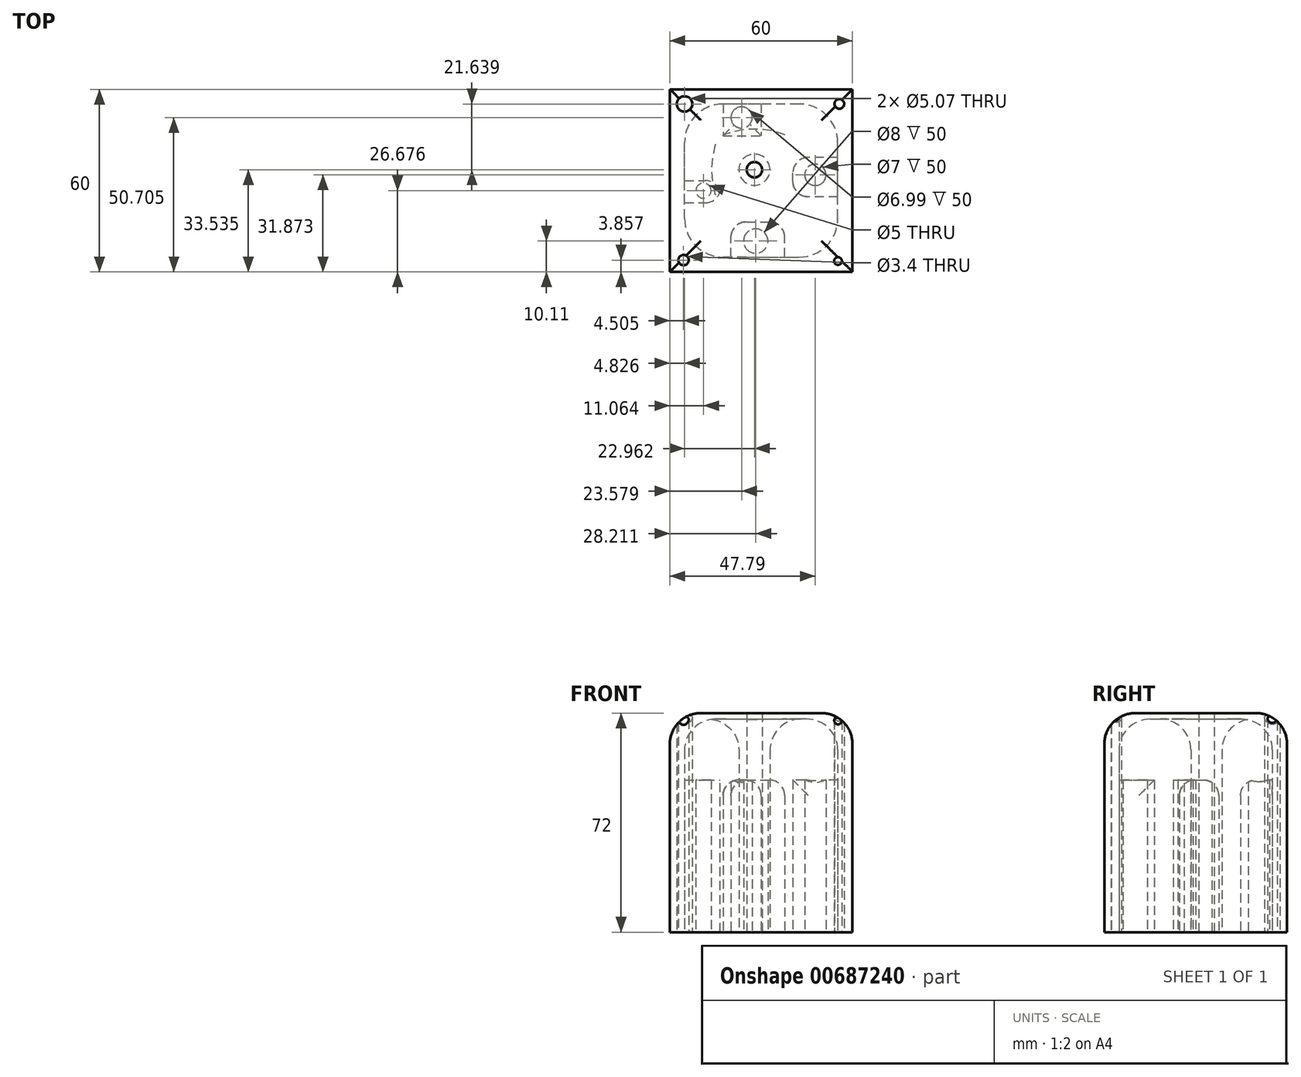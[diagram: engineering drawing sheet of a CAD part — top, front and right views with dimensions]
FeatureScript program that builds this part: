
annotation { "Feature Type Name" : "Feature", "Feature Type Description" : "" }
export const myFeature = defineFeature(function(context is Context, id is Id, definition is map)
    precondition{}
    {
        {
            var Q0;
            Q0=qCreatedBy(makeId("Top.planeOp"),FACE);
            var sketch = newSketch(context, id + "F0", { "sketchPlane" : qUnion([Q0])});
            skLineSegment(sketch, "E0.bottom", {"start": v(0, 0) * mm, "end": v(-60, 0) * mm});
            skLineSegment(sketch, "E0.top", {"start": v(0, 60) * mm, "end": v(-60, 60) * mm});
            skLineSegment(sketch, "E0.left", {"start": v(0, 0) * mm, "end": v(0, 60) * mm});
            skLineSegment(sketch, "E0.right", {"start": v(-60, 0) * mm, "end": v(-60, 60) * mm});
            skLineSegment(sketch, "E1.1", {"start": v(-4.83, 4.83) * mm, "end": v(-4.83, 24.65) * mm});
            skLineSegment(sketch, "E1.3", {"start": v(-55.17, 4.83) * mm, "end": v(-55.17, 22.68) * mm});
            skLineSegment(sketch, "E2.top", {"start": v(-39.92, 16.43) * mm, "end": v(-22.26, 16.43) * mm});
            skLineSegment(sketch, "E2.left", {"start": v(-39.92, 4.83) * mm, "end": v(-39.92, 16.43) * mm});
            skLineSegment(sketch, "E2.right", {"start": v(-22.26, 4.83) * mm, "end": v(-22.26, 16.43) * mm});
            skLineSegment(sketch, "E3.bottom", {"start": v(-4.83, 24.65) * mm, "end": v(-19.6, 24.65) * mm});
            skLineSegment(sketch, "E3.top", {"start": v(-4.83, 37.6) * mm, "end": v(-19.6, 37.6) * mm});
            skLineSegment(sketch, "E3.right", {"start": v(-19.6, 24.65) * mm, "end": v(-19.6, 37.6) * mm});
            skPoint(sketch, "E4.oppositeSnap0", {"position": v(-30, 55.17) * mm});
            skLineSegment(sketch, "E4.top", {"start": v(-42.54, 44.73) * mm, "end": v(-30, 44.73) * mm});
            skLineSegment(sketch, "E4.left", {"start": v(-42.54, 55.17) * mm, "end": v(-42.54, 44.73) * mm});
            skLineSegment(sketch, "E4.right", {"start": v(-30, 55.17) * mm, "end": v(-30, 44.73) * mm});
            skPoint(sketch, "E5.oppositeSnap0", {"position": v(-55.17, 30) * mm});
            skLineSegment(sketch, "E5.bottom", {"start": v(-55.17, 22.68) * mm, "end": v(-43.31, 22.68) * mm});
            skLineSegment(sketch, "E5.top", {"start": v(-55.17, 30) * mm, "end": v(-43.31, 30) * mm});
            skLineSegment(sketch, "E5.right", {"start": v(-43.31, 22.68) * mm, "end": v(-43.31, 30) * mm});
            skLineSegment(sketch, "E6.trimOffspring", {"start": v(-55.17, 30) * mm, "end": v(-55.17, 55.17) * mm});
            skLineSegment(sketch, "E7.trimOffspring", {"start": v(-39.92, 4.83) * mm, "end": v(-55.17, 4.83) * mm});
            skLineSegment(sketch, "E8.trimOffspring", {"start": v(-4.83, 37.6) * mm, "end": v(-4.83, 55.17) * mm});
            skLineSegment(sketch, "E9.trimOffspring", {"start": v(-42.54, 55.17) * mm, "end": v(-55.17, 55.17) * mm});
            skLineSegment(sketch, "E10", {"start": v(-22.26, 4.83) * mm, "end": v(-4.83, 4.83) * mm});
            skLineSegment(sketch, "E11", {"start": v(-4.83, 55.17) * mm, "end": v(-30, 55.17) * mm});
            skCircle(sketch, "E12", {"center": v(-31.79, 10.1) * mm, "radius": 4 * mm});
            skCircle(sketch, "E13", {"center": v(-12.21, 31.87) * mm, "radius": 3.5 * mm});
            skPoint(sketch, "E13.centerSnap0", {"position": v(-12.21, 24.65) * mm});
            skCircle(sketch, "E14", {"center": v(-36.42, 50.7) * mm, "radius": 3.5 * mm});
            skCircle(sketch, "E15", {"center": v(-48.94, 26.68) * mm, "radius": 2.5 * mm});
            skSolve(sketch);
        }
        {
            var Q0;
            Q0 = qSketchRegion(id + "F0", true);
            extrude(context, id + "F1", {"entities" : qUnion([Q0]), "depth" : 50 * mm, "offsetDistance" : 25.4 * mm});
        }
        {
            var Q0;
            Q0=makeQuery(id+"F1.opExtrude","SWEPT_EDGE",EDGE,{"disambiguationData":[OSD([sQuery(id+"F0.wireOp",EDGE,"E5.top"),sQuery(id+"F0.wireOp",EDGE,"E5.right")])]});
            var Q1;
            Q1=makeQuery(id+"F1.opExtrude","SWEPT_EDGE",EDGE,{"disambiguationData":[OSD([sQuery(id+"F0.wireOp",EDGE,"E5.bottom"),sQuery(id+"F0.wireOp",EDGE,"E5.right")])]});
            var Q2;
            Q2=makeQuery(id+"F1.opExtrude","CAP_EDGE",EDGE,{"disambiguationData":[OSD([sQuery(id+"F0.wireOp",EDGE,"E4.top")])],"isStart":false});
            var Q3;
            Q3=makeQuery(id+"F1.opExtrude","CAP_EDGE",EDGE,{"disambiguationData":[OSD([sQuery(id+"F0.wireOp",EDGE,"E3.top")])],"isStart":false});
            var Q4;
            Q4=makeQuery(id+"F1.opExtrude","CAP_EDGE",EDGE,{"disambiguationData":[OSD([sQuery(id+"F0.wireOp",EDGE,"E4.left")])],"isStart":false});
            var Q5;
            Q5=makeQuery(id+"F1.opExtrude","CAP_EDGE",EDGE,{"disambiguationData":[OSD([sQuery(id+"F0.wireOp",EDGE,"E4.right")])],"isStart":false});
            var Q6;
            Q6=makeQuery(id+"F1.opExtrude","SWEPT_EDGE",EDGE,{"disambiguationData":[OSD([sQuery(id+"F0.wireOp",EDGE,"E3.bottom"),sQuery(id+"F0.wireOp",EDGE,"E3.right")])]});
            var Q7;
            Q7=makeQuery(id+"F1.opExtrude","SWEPT_EDGE",EDGE,{"disambiguationData":[OSD([sQuery(id+"F0.wireOp",EDGE,"E3.top"),sQuery(id+"F0.wireOp",EDGE,"E3.right")])]});
            var Q8;
            Q8=makeQuery(id+"F1.opExtrude","CAP_EDGE",EDGE,{"disambiguationData":[OSD([sQuery(id+"F0.wireOp",EDGE,"E3.bottom")])],"isStart":false});
            var Q9;
            Q9=makeQuery(id+"F1.opExtrude","SWEPT_EDGE",EDGE,{"disambiguationData":[OSD([sQuery(id+"F0.wireOp",EDGE,"E2.top"),sQuery(id+"F0.wireOp",EDGE,"E2.left")])]});
            var Q10;
            Q10=makeQuery(id+"F1.opExtrude","SWEPT_EDGE",EDGE,{"disambiguationData":[OSD([sQuery(id+"F0.wireOp",EDGE,"E2.top"),sQuery(id+"F0.wireOp",EDGE,"E2.right")])]});
            var Q11;
            Q11=makeQuery(id+"F1.opExtrude","CAP_EDGE",EDGE,{"disambiguationData":[OSD([sQuery(id+"F0.wireOp",EDGE,"E2.right")])],"isStart":false});
            var Q12;
            Q12=makeQuery(id+"F1.opExtrude","CAP_EDGE",EDGE,{"disambiguationData":[OSD([sQuery(id+"F0.wireOp",EDGE,"E2.left")])],"isStart":false});
            fillet(context, id + "F2", {"entities" : qUnion([Q0, Q1, Q2, Q3, Q4, Q5, Q6, Q7, Q8, Q9, Q10, Q11, Q12]), "radius" : 5.08 * mm, "tangentPropagation" : true, "allowEdgeOverflow" : false});
        }
        {
            var Q0;
            Q0=makeQuery(id+"F2.opFillet","SPLIT",FACE,{"disambiguationData":[OD(1.0)],"derivedFrom":makeQuery(id+"F1.opExtrude","CAP_FACE",FACE,{"disambiguationData":[OSD([sQuery(id+"F0.wireOp",EDGE,"E0.bottom"),sQuery(id+"F0.wireOp",EDGE,"E0.top"),sQuery(id+"F0.wireOp",EDGE,"E0.left"),sQuery(id+"F0.wireOp",EDGE,"E0.right"),sQuery(id+"F0.wireOp",EDGE,"E1.1"),sQuery(id+"F0.wireOp",EDGE,"E1.3"),sQuery(id+"F0.wireOp",EDGE,"E2.top"),sQuery(id+"F0.wireOp",EDGE,"E2.left"),sQuery(id+"F0.wireOp",EDGE,"E2.right"),sQuery(id+"F0.wireOp",EDGE,"E3.bottom"),sQuery(id+"F0.wireOp",EDGE,"E3.top"),sQuery(id+"F0.wireOp",EDGE,"E3.right"),sQuery(id+"F0.wireOp",EDGE,"E4.top"),sQuery(id+"F0.wireOp",EDGE,"E4.left"),sQuery(id+"F0.wireOp",EDGE,"E4.right"),sQuery(id+"F0.wireOp",EDGE,"E5.bottom"),sQuery(id+"F0.wireOp",EDGE,"E5.top"),sQuery(id+"F0.wireOp",EDGE,"E5.right"),sQuery(id+"F0.wireOp",EDGE,"E6.trimOffspring"),sQuery(id+"F0.wireOp",EDGE,"E7.trimOffspring"),sQuery(id+"F0.wireOp",EDGE,"E8.trimOffspring"),sQuery(id+"F0.wireOp",EDGE,"E9.trimOffspring"),sQuery(id+"F0.wireOp",EDGE,"E10"),sQuery(id+"F0.wireOp",EDGE,"E11"),sQuery(id+"F0.wireOp",EDGE,"E12"),sQuery(id+"F0.wireOp",EDGE,"E13"),sQuery(id+"F0.wireOp",EDGE,"E14"),sQuery(id+"F0.wireOp",EDGE,"E15")])],"isStart":false})});
            var sketch = newSketch(context, id + "F3", { "sketchPlane" : qUnion([Q0])});
            skLineSegment(sketch, "E16.bottom", {"start": v(-60, 0) * mm, "end": v(0, 0) * mm});
            skLineSegment(sketch, "E16.top", {"start": v(-60, 60) * mm, "end": v(0, 60) * mm});
            skLineSegment(sketch, "E16.left", {"start": v(-60, 0) * mm, "end": v(-60, 60) * mm});
            skLineSegment(sketch, "E16.right", {"start": v(0, 0) * mm, "end": v(0, 60) * mm});
            skLineSegment(sketch, "E17.bottom", {"start": v(-55.17, 4.83) * mm, "end": v(-4.83, 4.83) * mm});
            skLineSegment(sketch, "E17.top", {"start": v(-55.17, 55.17) * mm, "end": v(-4.83, 55.17) * mm});
            skLineSegment(sketch, "E17.left", {"start": v(-55.17, 4.83) * mm, "end": v(-55.17, 55.17) * mm});
            skLineSegment(sketch, "E17.right", {"start": v(-4.83, 4.83) * mm, "end": v(-4.83, 55.17) * mm});
            skSolve(sketch);
        }
        {
            var Q0;
            Q0 = qSketchRegion(id + "F3", true);
            extrude(context, id + "F4", {"entities" : qUnion([Q0]), "operationType" : NewBodyOperationType.ADD, "depth" : 20 * mm, "offsetDistance" : 25.4 * mm});
        }
        {
            var Q0;
            Q0=makeQuery(id+"F4.opExtrude","CAP_FACE",FACE,{"disambiguationData":[OSD([sQuery(id+"F3.wireOp",EDGE,"E16.bottom"),sQuery(id+"F3.wireOp",EDGE,"E16.top"),sQuery(id+"F3.wireOp",EDGE,"E16.left"),sQuery(id+"F3.wireOp",EDGE,"E16.right"),sQuery(id+"F3.wireOp",EDGE,"E17.bottom"),sQuery(id+"F3.wireOp",EDGE,"E17.top"),sQuery(id+"F3.wireOp",EDGE,"E17.left"),sQuery(id+"F3.wireOp",EDGE,"E17.right")])],"isStart":false});
            var sketch = newSketch(context, id + "F5", { "sketchPlane" : qUnion([Q0])});
            skLineSegment(sketch, "E18.bottom", {"start": v(-60, 0) * mm, "end": v(0, 0) * mm});
            skLineSegment(sketch, "E18.top", {"start": v(-60, 60) * mm, "end": v(0, 60) * mm});
            skLineSegment(sketch, "E18.left", {"start": v(-60, 0) * mm, "end": v(-60, 60) * mm});
            skLineSegment(sketch, "E18.right", {"start": v(0, 0) * mm, "end": v(0, 60) * mm});
            skSolve(sketch);
        }
        {
            var Q0;
            Q0 = qSketchRegion(id + "F5", true);
            extrude(context, id + "F6", {"entities" : qUnion([Q0]), "operationType" : NewBodyOperationType.ADD, "depth" : 2 * mm, "offsetDistance" : 25.4 * mm});
        }
        {
            var Q0;
            Q0=qCreatedBy(makeId("Top.planeOp"),FACE);
            var sketch = newSketch(context, id + "F7", { "sketchPlane" : qUnion([Q0])});
            skCircle(sketch, "E19", {"center": v(-32.21, 33.53) * mm, "radius": 5.11 * mm});
            skSolve(sketch);
        }
        {
            var Q0;
            Q0 = qSketchRegion(id + "F7", true);
            extrude(context, id + "F8", {"entities" : qUnion([Q0]), "operationType" : NewBodyOperationType.ADD, "depth" : 70 * mm, "offsetDistance" : 25.4 * mm});
        }
        {
            var Q0;
            Q0=makeQuery(id+"F4.opExtrude","CAP_EDGE",EDGE,{"disambiguationData":[OSD([sQuery(id+"F3.wireOp",EDGE,"E17.right")])],"isStart":false});
            var Q1;
            Q1=makeQuery(id+"F4.opExtrude","CAP_EDGE",EDGE,{"disambiguationData":[OSD([sQuery(id+"F3.wireOp",EDGE,"E17.bottom")])],"isStart":false});
            var Q2;
            Q2=makeQuery(id+"F4.opExtrude","CAP_EDGE",EDGE,{"disambiguationData":[OSD([sQuery(id+"F3.wireOp",EDGE,"E17.left")])],"isStart":false});
            var Q3;
            Q3=makeQuery(id+"F6.opExtrude","CAP_EDGE",EDGE,{"disambiguationData":[OSD([sQuery(id+"F5.wireOp",EDGE,"E18.right")])],"isStart":false});
            var Q4;
            Q4=makeQuery(id+"F6.opExtrude","CAP_EDGE",EDGE,{"disambiguationData":[OSD([sQuery(id+"F5.wireOp",EDGE,"E18.top")])],"isStart":false});
            var Q5;
            Q5=makeQuery(id+"F6.opExtrude","CAP_EDGE",EDGE,{"disambiguationData":[OSD([sQuery(id+"F5.wireOp",EDGE,"E18.left")])],"isStart":false});
            var Q6;
            Q6=makeQuery(id+"F6.opExtrude","CAP_EDGE",EDGE,{"disambiguationData":[OSD([sQuery(id+"F5.wireOp",EDGE,"E18.bottom")])],"isStart":false});
            var Q7;
            Q7=makeQuery(id+"F6.opExtrude","CAP_FACE",FACE,{"disambiguationData":[OSD([sQuery(id+"F5.wireOp",EDGE,"E18.bottom"),sQuery(id+"F5.wireOp",EDGE,"E18.top"),sQuery(id+"F5.wireOp",EDGE,"E18.left"),sQuery(id+"F5.wireOp",EDGE,"E18.right")])],"isStart":true});
            fillet(context, id + "F9", {"entities" : qUnion([Q0, Q1, Q2, Q3, Q4, Q5, Q6, Q7]), "radius" : 10.16 * mm, "tangentPropagation" : true, "allowEdgeOverflow" : false});
        }
        {
            var Q0;
            Q0=makeQuery(id+"F4.boolean.opBoolean","MERGE",EDGE,{"derivedFrom":[makeQuery(id+"F1.opExtrude","SWEPT_EDGE",EDGE,{"disambiguationData":[OSD([sQuery(id+"F0.wireOp",EDGE,"E1.3"),sQuery(id+"F0.wireOp",EDGE,"E7.trimOffspring")])]}),makeQuery(id+"F4.opExtrude","SWEPT_EDGE",EDGE,{"disambiguationData":[OSD([sQuery(id+"F3.wireOp",EDGE,"E17.bottom"),sQuery(id+"F3.wireOp",EDGE,"E17.left")])]})]});
            fillet(context, id + "F10", {"entities" : qUnion([Q0]), "radius" : 12.7 * mm, "tangentPropagation" : true, "allowEdgeOverflow" : false});
        }
        {
            var Q0;
            Q0=makeQuery(id+"F4.boolean.opBoolean","MERGE",EDGE,{"derivedFrom":[makeQuery(id+"F1.opExtrude","SWEPT_EDGE",EDGE,{"disambiguationData":[OSD([sQuery(id+"F0.wireOp",EDGE,"E1.1"),sQuery(id+"F0.wireOp",EDGE,"E10")])]}),makeQuery(id+"F4.opExtrude","SWEPT_EDGE",EDGE,{"disambiguationData":[OSD([sQuery(id+"F3.wireOp",EDGE,"E17.bottom"),sQuery(id+"F3.wireOp",EDGE,"E17.right")])]})]});
            fillet(context, id + "F11", {"entities" : qUnion([Q0]), "radius" : 12.7 * mm, "tangentPropagation" : true, "allowEdgeOverflow" : false});
        }
        {
            var Q0;
            Q0=makeQuery(id+"F4.boolean.opBoolean","MERGE",EDGE,{"derivedFrom":[makeQuery(id+"F1.opExtrude","SWEPT_EDGE",EDGE,{"disambiguationData":[OSD([sQuery(id+"F0.wireOp",EDGE,"E8.trimOffspring"),sQuery(id+"F0.wireOp",EDGE,"E11")])]}),makeQuery(id+"F4.opExtrude","SWEPT_EDGE",EDGE,{"disambiguationData":[OSD([sQuery(id+"F3.wireOp",EDGE,"E17.top"),sQuery(id+"F3.wireOp",EDGE,"E17.right")])]})]});
            fillet(context, id + "F12", {"entities" : qUnion([Q0]), "radius" : 12.7 * mm, "tangentPropagation" : true, "allowEdgeOverflow" : false});
        }
        {
            var Q0;
            Q0=makeQuery(id+"F4.boolean.opBoolean","MERGE",EDGE,{"derivedFrom":[makeQuery(id+"F1.opExtrude","SWEPT_EDGE",EDGE,{"disambiguationData":[OSD([sQuery(id+"F0.wireOp",EDGE,"E6.trimOffspring"),sQuery(id+"F0.wireOp",EDGE,"E9.trimOffspring")])]}),makeQuery(id+"F4.opExtrude","SWEPT_EDGE",EDGE,{"disambiguationData":[OSD([sQuery(id+"F3.wireOp",EDGE,"E17.top"),sQuery(id+"F3.wireOp",EDGE,"E17.left")])]})]});
            fillet(context, id + "F13", {"entities" : qUnion([Q0]), "radius" : 12.7 * mm, "tangentPropagation" : true, "allowEdgeOverflow" : false});
        }
        {
            var Q0;
            Q0=makeQuery(id+"F1.opExtrude","CAP_FACE",FACE,{"disambiguationData":[OSD([sQuery(id+"F0.wireOp",EDGE,"E0.bottom"),sQuery(id+"F0.wireOp",EDGE,"E0.top"),sQuery(id+"F0.wireOp",EDGE,"E0.left"),sQuery(id+"F0.wireOp",EDGE,"E0.right"),sQuery(id+"F0.wireOp",EDGE,"E1.1"),sQuery(id+"F0.wireOp",EDGE,"E1.3"),sQuery(id+"F0.wireOp",EDGE,"E2.top"),sQuery(id+"F0.wireOp",EDGE,"E2.left"),sQuery(id+"F0.wireOp",EDGE,"E2.right"),sQuery(id+"F0.wireOp",EDGE,"E3.bottom"),sQuery(id+"F0.wireOp",EDGE,"E3.top"),sQuery(id+"F0.wireOp",EDGE,"E3.right"),sQuery(id+"F0.wireOp",EDGE,"E4.top"),sQuery(id+"F0.wireOp",EDGE,"E4.left"),sQuery(id+"F0.wireOp",EDGE,"E4.right"),sQuery(id+"F0.wireOp",EDGE,"E5.bottom"),sQuery(id+"F0.wireOp",EDGE,"E5.top"),sQuery(id+"F0.wireOp",EDGE,"E5.right"),sQuery(id+"F0.wireOp",EDGE,"E6.trimOffspring"),sQuery(id+"F0.wireOp",EDGE,"E7.trimOffspring"),sQuery(id+"F0.wireOp",EDGE,"E8.trimOffspring"),sQuery(id+"F0.wireOp",EDGE,"E9.trimOffspring"),sQuery(id+"F0.wireOp",EDGE,"E10"),sQuery(id+"F0.wireOp",EDGE,"E11"),sQuery(id+"F0.wireOp",EDGE,"E12"),sQuery(id+"F0.wireOp",EDGE,"E13"),sQuery(id+"F0.wireOp",EDGE,"E14"),sQuery(id+"F0.wireOp",EDGE,"E15")])],"isStart":true});
            var sketch = newSketch(context, id + "F14", { "sketchPlane" : qUnion([Q0])});
            skCircle(sketch, "E20", {"center": v(-55.5, -3.86) * mm, "radius": 1.7 * mm});
            skCircle(sketch, "E21", {"center": v(-4.77, -3.56) * mm, "radius": 1.27 * mm});
            skCircle(sketch, "E22", {"center": v(-4.32, -55.17) * mm, "radius": 1.59 * mm});
            skCircle(sketch, "E23", {"center": v(-55.17, -55.17) * mm, "radius": 2.54 * mm});
            skSolve(sketch);
        }
        {
            var Q0;
            Q0 = qSketchRegion(id + "F14", true);
            extrude(context, id + "F15", {"entities" : qUnion([Q0]), "operationType" : NewBodyOperationType.REMOVE, "endBound" : BoundingType.THROUGH_ALL, "oppositeDirection" : true, "depth" : 25.4 * mm, "offsetDistance" : 25.4 * mm});
        }
        {
            var Q0;
            Q0=makeQuery(id+"F8.opExtrude","CAP_FACE",FACE,{"disambiguationData":[OSD([sQuery(id+"F7.wireOp",EDGE,"E19")])],"isStart":true});
            var sketch = newSketch(context, id + "F16", { "sketchPlane" : qUnion([Q0])});
            skCircle(sketch, "E24", {"center": v(-32.21, -33.53) * mm, "radius": 2.53 * mm});
            skSolve(sketch);
        }
        {
            var Q0;
            Q0 = qSketchRegion(id + "F16", true);
            extrude(context, id + "F17", {"entities" : qUnion([Q0]), "operationType" : NewBodyOperationType.REMOVE, "endBound" : BoundingType.THROUGH_ALL, "oppositeDirection" : true, "depth" : 25.4 * mm, "offsetDistance" : 25.4 * mm});
        }
    });
